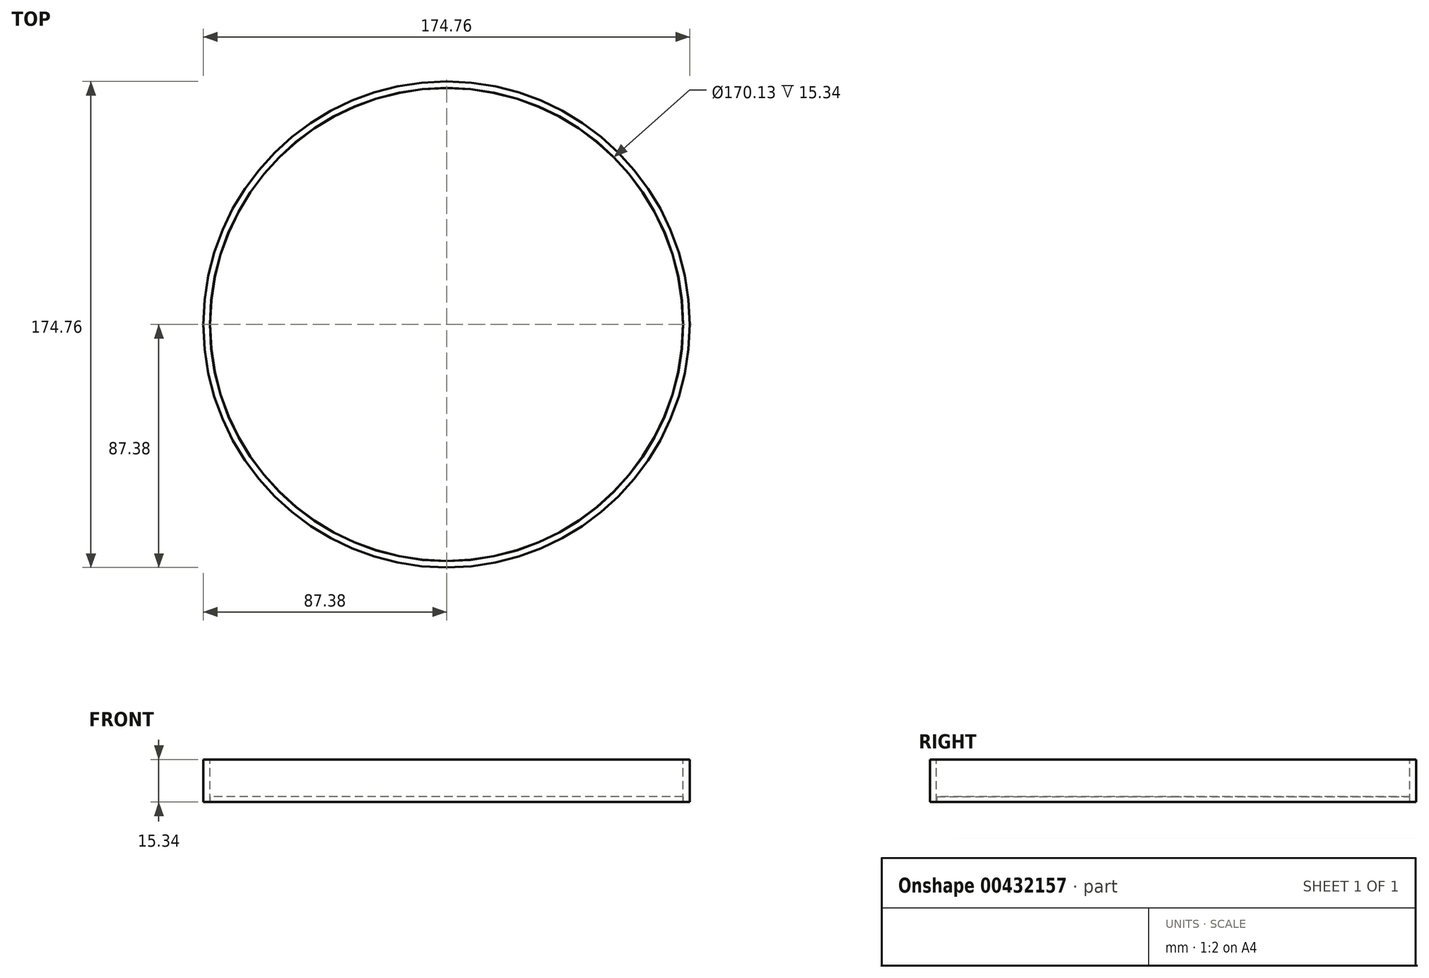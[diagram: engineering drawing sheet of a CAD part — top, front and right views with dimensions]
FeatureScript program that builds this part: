
annotation { "Feature Type Name" : "Feature", "Feature Type Description" : "" }
export const myFeature = defineFeature(function(context is Context, id is Id, definition is map)
    precondition{}
    {
        {
            var Q0;
            Q0=qCreatedBy(makeId("Top.planeOp"),FACE);
            var sketch = newSketch(context, id + "F0", { "sketchPlane" : qUnion([Q0])});
            skCircle(sketch, "E0", {"center": v(0, 0) * mm, "radius": 85 * mm});
            skSolve(sketch);
        }
        {
            var Q0;
            Q0=makeQuery(id+"F0.imprint","IMPRINT",FACE,{"disambiguationData":[TD([[makeQuery(id+"F0.imprint","IMPRINT",EDGE,{"derivedFrom":sQuery(id+"F0.wireOp",EDGE,"E0")}),1.0]])]});
            extrude(context, id + "F1", {"entities" : qUnion([Q0]), "depth" : 2 * mm});
        }
        {
            var Q0;
            Q0=qCreatedBy(makeId("Right.planeOp"),FACE);
            var sketch = newSketch(context, id + "F2", { "sketchPlane" : qUnion([Q0])});
            skLineSegment(sketch, "E1.bottom", {"start": v(-85.07, 0) * mm, "end": v(-87.38, 0) * mm});
            skLineSegment(sketch, "E1.top", {"start": v(-85.07, 15.34) * mm, "end": v(-87.38, 15.34) * mm});
            skLineSegment(sketch, "E1.left", {"start": v(-85.07, 0) * mm, "end": v(-85.07, 15.34) * mm});
            skLineSegment(sketch, "E1.right", {"start": v(-87.38, 0) * mm, "end": v(-87.38, 15.34) * mm});
            skSolve(sketch);
        }
        {
            var Q0;
            Q0 = qSketchRegion(id + "F2", true);
            var Q1;
            Q1=makeQuery(id+"F1.opExtrude","CAP_EDGE",EDGE,{"disambiguationData":[OSD([sQuery(id+"F0.wireOp",EDGE,"E0")])],"isStart":false});
            sweep(context, id + "F3", {"profiles" : qUnion([Q0]), "path" : qUnion([Q1])});
        }
    });
